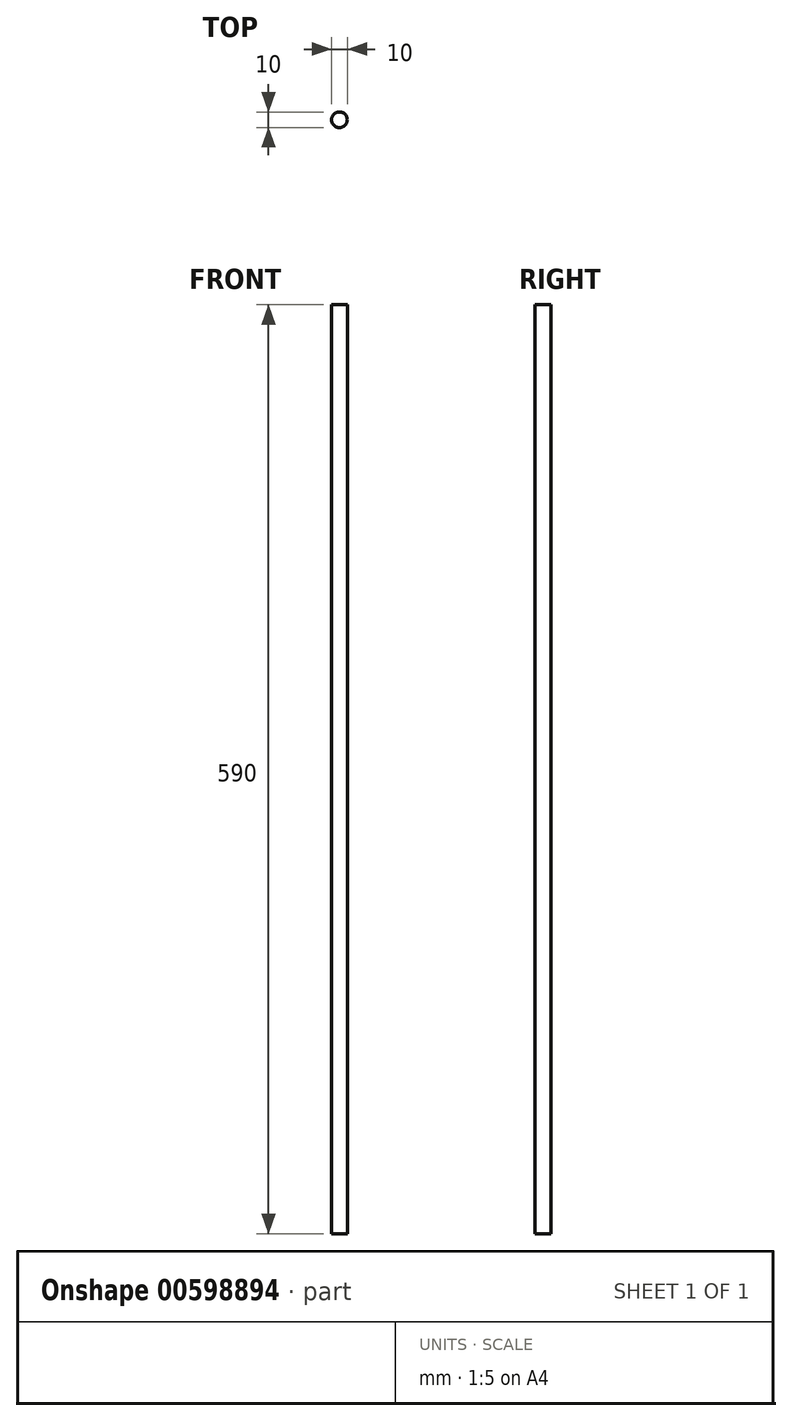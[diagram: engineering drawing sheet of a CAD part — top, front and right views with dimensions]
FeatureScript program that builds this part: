
annotation { "Feature Type Name" : "Feature", "Feature Type Description" : "" }
export const myFeature = defineFeature(function(context is Context, id is Id, definition is map)
    precondition{}
    {
        {
            var Q0;
            Q0=qCreatedBy(makeId("Top.planeOp"),FACE);
            var sketch = newSketch(context, id + "F0", { "sketchPlane" : qUnion([Q0])});
            skCircle(sketch, "E0", {"center": v(0, 0) * mm, "radius": 5 * mm});
            skSolve(sketch);
        }
        {
            var Q0;
            Q0=qSketchRegion(id+"F0",true);
            extrude(context, id + "F1", {"entities" : qUnion([Q0]), "depth" : 590 * mm, "offsetDistance" : 25 * mm});
        }
    });
